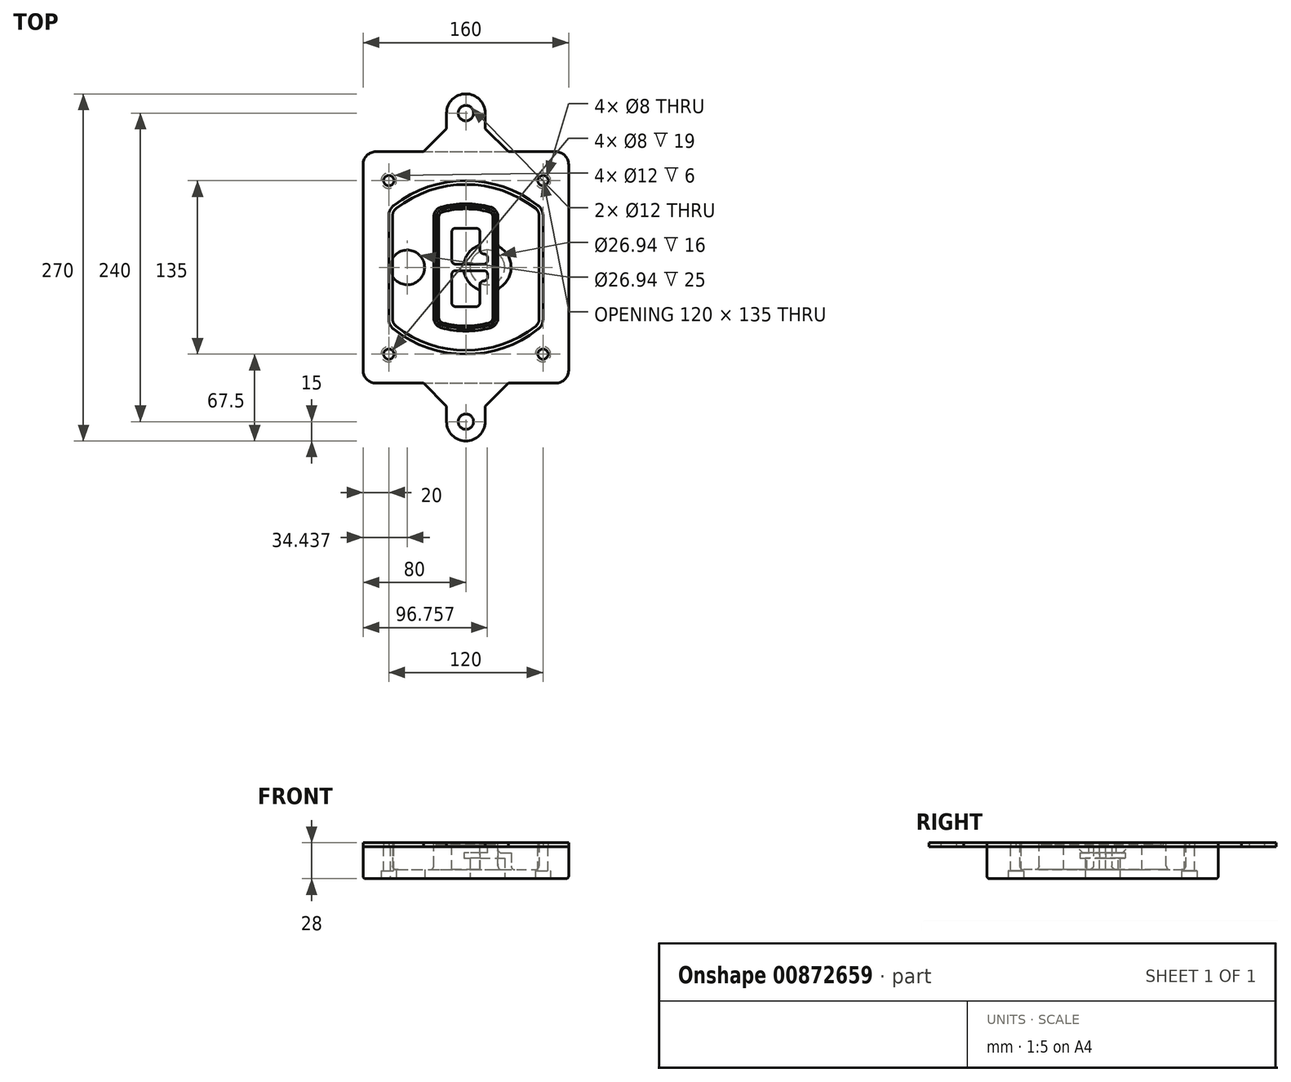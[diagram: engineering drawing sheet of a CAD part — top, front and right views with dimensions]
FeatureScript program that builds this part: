
annotation { "Feature Type Name" : "Feature", "Feature Type Description" : "" }
export const myFeature = defineFeature(function(context is Context, id is Id, definition is map)
    precondition{}
    {
        {
            var Q0;
            Q0=qCreatedBy(makeId("Top.planeOp"),FACE);
            var sketch = newSketch(context, id + "F0", { "sketchPlane" : qUnion([Q0])});
            skPoint(sketch, "E0.rect.middle", {"position": v(0, 0) * mm});
            skLineSegment(sketch, "E1.bottom", {"start": v(-70, -90) * mm, "end": v(70, -90) * mm});
            skLineSegment(sketch, "E1.top", {"start": v(-70, 90) * mm, "end": v(70, 90) * mm});
            skLineSegment(sketch, "E1.left", {"start": v(-80, -80) * mm, "end": v(-80, 80) * mm});
            skLineSegment(sketch, "E1.right", {"start": v(80, -80) * mm, "end": v(80, 80) * mm});
            skLineSegment(sketch, "E2", {"start": v(-80, 90) * mm, "end": v(80, -90) * mm, "construction": true});
            skLineSegment(sketch, "E3", {"start": v(80, 90) * mm, "end": v(-80, -90) * mm, "construction": true});
            skCircle(sketch, "E4", {"center": v(-60, 67.5) * mm, "radius": 4 * mm});
            skCircle(sketch, "E5", {"center": v(60, 67.5) * mm, "radius": 4 * mm});
            skCircle(sketch, "E6", {"center": v(60, -67.5) * mm, "radius": 4 * mm});
            skCircle(sketch, "E7", {"center": v(-60, -67.5) * mm, "radius": 4 * mm});
            skLineSegment(sketch, "E8", {"start": v(-60, 67.5) * mm, "end": v(60, 67.5) * mm, "construction": true});
            skLineSegment(sketch, "E9", {"start": v(60, 67.5) * mm, "end": v(60, -67.5) * mm, "construction": true});
            skLineSegment(sketch, "E10", {"start": v(60, -67.5) * mm, "end": v(-60, -67.5) * mm, "construction": true});
            skLineSegment(sketch, "E11", {"start": v(-60, -67.5) * mm, "end": v(-60, 67.5) * mm, "construction": true});
            skLineSegment(sketch, "E12", {"start": v(-60, 40.3) * mm, "end": v(-60, -40.3) * mm});
            skLineSegment(sketch, "E13", {"start": v(60, 40.3) * mm, "end": v(60, -40.3) * mm});
            skArc(sketch, "E14", {"start": v(56.15, 48.18) * mm, "mid": v(0, 67.5) * mm, "end": v(-56.15, 48.18) * mm});
            skArc(sketch, "E15", {"start": v(-56.15, -48.18) * mm, "mid": v(0, -67.5) * mm, "end": v(56.15, -48.18) * mm});
            skLineSegment(sketch, "E16", {"start": v(-60, 0) * mm, "end": v(60, 0) * mm, "construction": true});
            skPoint(sketch, "E17.visualSharp", {"position": v(-60, -45) * mm});
            skArc(sketch, "E17.filletArc", {"start": v(-60, -40.3) * mm, "mid": v(-58.99, -44.68) * mm, "end": v(-56.15, -48.18) * mm});
            skPoint(sketch, "E18.visualSharp", {"position": v(-60, 45) * mm});
            skArc(sketch, "E18.filletArc", {"start": v(-56.15, 48.18) * mm, "mid": v(-58.99, 44.68) * mm, "end": v(-60, 40.3) * mm});
            skPoint(sketch, "E19.visualSharp", {"position": v(60, 45) * mm});
            skArc(sketch, "E19.filletArc", {"start": v(60, 40.3) * mm, "mid": v(58.99, 44.68) * mm, "end": v(56.15, 48.18) * mm});
            skPoint(sketch, "E20.visualSharp", {"position": v(60, -45) * mm});
            skArc(sketch, "E20.filletArc", {"start": v(56.15, -48.18) * mm, "mid": v(58.99, -44.68) * mm, "end": v(60, -40.3) * mm});
            skPoint(sketch, "E21.visualSharp", {"position": v(-80, 90) * mm});
            skArc(sketch, "E21.filletArc", {"start": v(-70, 90) * mm, "mid": v(-77.07, 87.07) * mm, "end": v(-80, 80) * mm});
            skPoint(sketch, "E22.visualSharp", {"position": v(80, 90) * mm});
            skArc(sketch, "E22.filletArc", {"start": v(80, 80) * mm, "mid": v(77.07, 87.07) * mm, "end": v(70, 90) * mm});
            skPoint(sketch, "E23.visualSharp", {"position": v(80, -90) * mm});
            skArc(sketch, "E23.filletArc", {"start": v(70, -90) * mm, "mid": v(77.07, -87.07) * mm, "end": v(80, -80) * mm});
            skPoint(sketch, "E24.visualSharp", {"position": v(-80, -90) * mm});
            skArc(sketch, "E24.filletArc", {"start": v(-80, -80) * mm, "mid": v(-77.07, -87.07) * mm, "end": v(-70, -90) * mm});
            skArc(sketch, "E25.0", {"start": v(57, 40.3) * mm, "mid": v(56.3, 43.36) * mm, "end": v(54.3, 45.81) * mm});
            skLineSegment(sketch, "E25.1", {"start": v(57, 40.3) * mm, "end": v(57, -40.3) * mm});
            skArc(sketch, "E25.2", {"start": v(54.3, -45.81) * mm, "mid": v(56.3, -43.36) * mm, "end": v(57, -40.3) * mm});
            skArc(sketch, "E25.3", {"start": v(-54.3, -45.81) * mm, "mid": v(0, -64.5) * mm, "end": v(54.3, -45.81) * mm});
            skArc(sketch, "E25.4", {"start": v(-57, -40.3) * mm, "mid": v(-56.3, -43.36) * mm, "end": v(-54.3, -45.81) * mm});
            skArc(sketch, "E25.5", {"start": v(54.3, 45.81) * mm, "mid": v(0, 64.5) * mm, "end": v(-54.3, 45.81) * mm});
            skLineSegment(sketch, "E25.6", {"start": v(-57, 40.3) * mm, "end": v(-57, -40.3) * mm});
            skArc(sketch, "E25.7", {"start": v(-54.3, 45.81) * mm, "mid": v(-56.3, 43.36) * mm, "end": v(-57, 40.3) * mm});
            skArc(sketch, "E26.0", {"start": v(-58.62, 51.33) * mm, "mid": v(-62.58, 46.43) * mm, "end": v(-64, 40.3) * mm});
            skArc(sketch, "E26.1", {"start": v(58.62, 51.33) * mm, "mid": v(0, 71.5) * mm, "end": v(-58.62, 51.33) * mm});
            skArc(sketch, "E26.2", {"start": v(64, 40.3) * mm, "mid": v(62.58, 46.43) * mm, "end": v(58.62, 51.33) * mm});
            skLineSegment(sketch, "E26.3", {"start": v(64, 40.3) * mm, "end": v(64, -40.3) * mm});
            skArc(sketch, "E26.4", {"start": v(58.62, -51.33) * mm, "mid": v(62.58, -46.43) * mm, "end": v(64, -40.3) * mm});
            skLineSegment(sketch, "E26.5", {"start": v(-64, 40.3) * mm, "end": v(-64, -40.3) * mm});
            skArc(sketch, "E26.6", {"start": v(-58.62, -51.33) * mm, "mid": v(0, -71.5) * mm, "end": v(58.62, -51.33) * mm});
            skArc(sketch, "E26.7", {"start": v(-64, -40.3) * mm, "mid": v(-62.58, -46.43) * mm, "end": v(-58.62, -51.33) * mm});
            skSolve(sketch);
        }
        {
            var Q0;
            Q0=makeQuery(id+"F0.imprint","IMPRINT",FACE,{"disambiguationData":[TD([[makeQuery(id+"F0.imprint","IMPRINT",EDGE,{"derivedFrom":sQuery(id+"F0.wireOp",EDGE,"E1.bottom")}),1.0]])]});
            var Q1;
            Q1=makeQuery(id+"F0.imprint","IMPRINT",FACE,{"disambiguationData":[TD([[makeQuery(id+"F0.imprint","IMPRINT",EDGE,{"derivedFrom":sQuery(id+"F0.wireOp",EDGE,"E12")}),1.0]])]});
            var Q2;
            Q2=makeQuery(id+"F0.imprint","IMPRINT",FACE,{"disambiguationData":[TD([[makeQuery(id+"F0.imprint","IMPRINT",EDGE,{"derivedFrom":sQuery(id+"F0.wireOp",EDGE,"E25.0")}),1.0]])]});
            var Q3;
            Q3=makeQuery(id+"F0.imprint","IMPRINT",FACE,{"disambiguationData":[TD([[makeQuery(id+"F0.imprint","IMPRINT",EDGE,{"derivedFrom":sQuery(id+"F0.wireOp",EDGE,"E12")}),-1.0]])]});
            extrude(context, id + "F1", {"entities" : qUnion([Q0, Q1, Q2, Q3]), "oppositeDirection" : true, "depth" : 25 * mm});
        }
        {
            var Q0;
            Q0=makeQuery(id+"F0.imprint","IMPRINT",FACE,{"disambiguationData":[TD([[makeQuery(id+"F0.imprint","IMPRINT",EDGE,{"derivedFrom":sQuery(id+"F0.wireOp",EDGE,"E12")}),1.0]])]});
            extrude(context, id + "F2", {"entities" : qUnion([Q0]), "operationType" : NewBodyOperationType.ADD, "depth" : 3 * mm});
        }
        {
            var Q0;
            Q0=makeQuery(id+"F0.imprint","IMPRINT",FACE,{"disambiguationData":[TD([[makeQuery(id+"F0.imprint","IMPRINT",EDGE,{"derivedFrom":sQuery(id+"F0.wireOp",EDGE,"E25.0")}),1.0]])]});
            extrude(context, id + "F3", {"entities" : qUnion([Q0]), "operationType" : NewBodyOperationType.REMOVE, "oppositeDirection" : true, "depth" : 18 * mm});
        }
        {
            var Q0;
            Q0=makeQuery(id+"F2.opExtrude","CAP_FACE",FACE,{"disambiguationData":[OSD([sQuery(id+"F0.wireOp",EDGE,"E12"),sQuery(id+"F0.wireOp",EDGE,"E13"),sQuery(id+"F0.wireOp",EDGE,"E14"),sQuery(id+"F0.wireOp",EDGE,"E15"),sQuery(id+"F0.wireOp",EDGE,"E17.filletArc"),sQuery(id+"F0.wireOp",EDGE,"E18.filletArc"),sQuery(id+"F0.wireOp",EDGE,"E19.filletArc"),sQuery(id+"F0.wireOp",EDGE,"E20.filletArc"),sQuery(id+"F0.wireOp",EDGE,"E25.0"),sQuery(id+"F0.wireOp",EDGE,"E25.1"),sQuery(id+"F0.wireOp",EDGE,"E25.2"),sQuery(id+"F0.wireOp",EDGE,"E25.3"),sQuery(id+"F0.wireOp",EDGE,"E25.4"),sQuery(id+"F0.wireOp",EDGE,"E25.5"),sQuery(id+"F0.wireOp",EDGE,"E25.6"),sQuery(id+"F0.wireOp",EDGE,"E25.7")])],"isStart":false});
            var sketch = newSketch(context, id + "F4", { "sketchPlane" : qUnion([Q0])});
            skArc(sketch, "E27.0", {"start": v(-19.08, -46.97) * mm, "mid": v(0, -49.5) * mm, "end": v(19.08, -46.97) * mm});
            skArc(sketch, "E28.0", {"start": v(19.08, 46.97) * mm, "mid": v(0, 49.5) * mm, "end": v(-19.08, 46.97) * mm});
            skLineSegment(sketch, "E29", {"start": v(-25, 39.25) * mm, "end": v(-25, -39.25) * mm});
            skLineSegment(sketch, "E30", {"start": v(25, 39.25) * mm, "end": v(25, -39.25) * mm});
            skLineSegment(sketch, "E31", {"start": v(-25, 45.1) * mm, "end": v(25, 45.1) * mm, "construction": true});
            skLineSegment(sketch, "E32", {"start": v(-25, -45.1) * mm, "end": v(25, -45.1) * mm, "construction": true});
            skPoint(sketch, "E33.visualSharp", {"position": v(-25, 45.1) * mm});
            skArc(sketch, "E33.filletArc", {"start": v(-19.08, 46.97) * mm, "mid": v(-23.35, 44.11) * mm, "end": v(-25, 39.25) * mm});
            skPoint(sketch, "E34.visualSharp", {"position": v(25, 45.1) * mm});
            skArc(sketch, "E34.filletArc", {"start": v(25, 39.25) * mm, "mid": v(23.35, 44.11) * mm, "end": v(19.08, 46.97) * mm});
            skPoint(sketch, "E35.visualSharp", {"position": v(25, -45.1) * mm});
            skArc(sketch, "E35.filletArc", {"start": v(19.08, -46.97) * mm, "mid": v(23.35, -44.11) * mm, "end": v(25, -39.25) * mm});
            skPoint(sketch, "E36.visualSharp", {"position": v(-25, -45.1) * mm});
            skArc(sketch, "E36.filletArc", {"start": v(-25, -39.25) * mm, "mid": v(-23.35, -44.11) * mm, "end": v(-19.08, -46.97) * mm});
            skArc(sketch, "E37.0", {"start": v(54.3, 45.81) * mm, "mid": v(0, 64.5) * mm, "end": v(-54.3, 45.81) * mm});
            skArc(sketch, "E37.1", {"start": v(-54.3, 45.81) * mm, "mid": v(-56.3, 43.36) * mm, "end": v(-57, 40.3) * mm});
            skLineSegment(sketch, "E37.2", {"start": v(-57, 40.3) * mm, "end": v(-57, -40.3) * mm});
            skArc(sketch, "E37.3", {"start": v(-57, -40.3) * mm, "mid": v(-56.3, -43.36) * mm, "end": v(-54.3, -45.81) * mm});
            skArc(sketch, "E37.4", {"start": v(-54.3, -45.81) * mm, "mid": v(0, -64.5) * mm, "end": v(54.3, -45.81) * mm});
            skArc(sketch, "E37.5", {"start": v(54.3, -45.81) * mm, "mid": v(56.3, -43.36) * mm, "end": v(57, -40.3) * mm});
            skLineSegment(sketch, "E37.6", {"start": v(57, 40.3) * mm, "end": v(57, -40.3) * mm});
            skArc(sketch, "E37.7", {"start": v(57, 40.3) * mm, "mid": v(56.3, 43.36) * mm, "end": v(54.3, 45.81) * mm});
            skLineSegment(sketch, "E38.0", {"start": v(23, 39.25) * mm, "end": v(23, -39.25) * mm});
            skArc(sketch, "E38.1", {"start": v(18.56, -45.04) * mm, "mid": v(21.76, -42.9) * mm, "end": v(23, -39.25) * mm});
            skArc(sketch, "E38.2", {"start": v(-18.56, -45.04) * mm, "mid": v(0, -47.5) * mm, "end": v(18.56, -45.04) * mm});
            skArc(sketch, "E38.3", {"start": v(-23, -39.25) * mm, "mid": v(-21.76, -42.9) * mm, "end": v(-18.56, -45.04) * mm});
            skLineSegment(sketch, "E38.4", {"start": v(-23, 39.25) * mm, "end": v(-23, -39.25) * mm});
            skArc(sketch, "E38.5", {"start": v(23, 39.25) * mm, "mid": v(21.76, 42.9) * mm, "end": v(18.56, 45.04) * mm});
            skArc(sketch, "E38.6", {"start": v(-18.56, 45.04) * mm, "mid": v(-21.76, 42.9) * mm, "end": v(-23, 39.25) * mm});
            skArc(sketch, "E38.7", {"start": v(18.56, 45.04) * mm, "mid": v(0, 47.5) * mm, "end": v(-18.56, 45.04) * mm});
            skArc(sketch, "E39.0", {"start": v(21, 39.25) * mm, "mid": v(20.18, 41.68) * mm, "end": v(18.04, 43.1) * mm});
            skLineSegment(sketch, "E39.1", {"start": v(21, 39.25) * mm, "end": v(21, -39.25) * mm});
            skArc(sketch, "E39.2", {"start": v(18.04, -43.1) * mm, "mid": v(20.18, -41.68) * mm, "end": v(21, -39.25) * mm});
            skArc(sketch, "E39.3", {"start": v(-18.04, -43.1) * mm, "mid": v(0, -45.5) * mm, "end": v(18.04, -43.1) * mm});
            skArc(sketch, "E39.4", {"start": v(-21, -39.25) * mm, "mid": v(-20.18, -41.68) * mm, "end": v(-18.04, -43.1) * mm});
            skArc(sketch, "E39.5", {"start": v(18.04, 43.1) * mm, "mid": v(0, 45.5) * mm, "end": v(-18.04, 43.1) * mm});
            skLineSegment(sketch, "E39.6", {"start": v(-21, 39.25) * mm, "end": v(-21, -39.25) * mm});
            skArc(sketch, "E39.7", {"start": v(-18.04, 43.1) * mm, "mid": v(-20.18, 41.68) * mm, "end": v(-21, 39.25) * mm});
            skLineSegment(sketch, "E40", {"start": v(-25, 0) * mm, "end": v(25, 0) * mm, "construction": true});
            skLineSegment(sketch, "E41", {"start": v(-11, 5.5) * mm, "end": v(-11, 27.5) * mm});
            skLineSegment(sketch, "E42", {"start": v(-8, 30.5) * mm, "end": v(8, 30.5) * mm});
            skLineSegment(sketch, "E43", {"start": v(11, 27.5) * mm, "end": v(11, 13.5) * mm});
            skLineSegment(sketch, "E44", {"start": v(14, 10.5) * mm, "end": v(14, 10.5) * mm});
            skLineSegment(sketch, "E45", {"start": v(17, 7.5) * mm, "end": v(17, 5.5) * mm});
            skLineSegment(sketch, "E46", {"start": v(14, 2.5) * mm, "end": v(-8, 2.5) * mm});
            skPoint(sketch, "E47.visualSharp", {"position": v(-11, 30.5) * mm});
            skArc(sketch, "E47.filletArc", {"start": v(-8, 30.5) * mm, "mid": v(-10.12, 29.62) * mm, "end": v(-11, 27.5) * mm});
            skPoint(sketch, "E48.visualSharp", {"position": v(11, 30.5) * mm});
            skArc(sketch, "E48.filletArc", {"start": v(11, 27.5) * mm, "mid": v(10.12, 29.62) * mm, "end": v(8, 30.5) * mm});
            skPoint(sketch, "E49.visualSharp", {"position": v(11, 10.5) * mm});
            skArc(sketch, "E49.filletArc", {"start": v(11, 13.5) * mm, "mid": v(11.88, 11.38) * mm, "end": v(14, 10.5) * mm});
            skPoint(sketch, "E50.visualSharp", {"position": v(17, 10.5) * mm});
            skArc(sketch, "E50.filletArc", {"start": v(17, 7.5) * mm, "mid": v(16.12, 9.62) * mm, "end": v(14, 10.5) * mm});
            skPoint(sketch, "E51.visualSharp", {"position": v(17, 2.5) * mm});
            skArc(sketch, "E51.filletArc", {"start": v(14, 2.5) * mm, "mid": v(16.12, 3.38) * mm, "end": v(17, 5.5) * mm});
            skPoint(sketch, "E52.visualSharp", {"position": v(-11, 2.5) * mm});
            skArc(sketch, "E52.filletArc", {"start": v(-11, 5.5) * mm, "mid": v(-10.12, 3.38) * mm, "end": v(-8, 2.5) * mm});
            skLineSegment(sketch, "E53.0.MirrorCS", {"start": v(14, -2.5) * mm, "end": v(-8, -2.5) * mm});
            skArc(sketch, "E54.0.MirrorCS", {"start": v(-11, -5.5) * mm, "mid": v(-10.12, -3.38) * mm, "end": v(-8, -2.5) * mm});
            skLineSegment(sketch, "E55.0.MirrorCS", {"start": v(-11, -5.5) * mm, "end": v(-11, -27.5) * mm});
            skArc(sketch, "E56.0.MirrorCS", {"start": v(-8, -30.5) * mm, "mid": v(-10.12, -29.62) * mm, "end": v(-11, -27.5) * mm});
            skLineSegment(sketch, "E57.0.MirrorCS", {"start": v(-8, -30.5) * mm, "end": v(8, -30.5) * mm});
            skArc(sketch, "E58.0.MirrorCS", {"start": v(11, -27.5) * mm, "mid": v(10.12, -29.62) * mm, "end": v(8, -30.5) * mm});
            skLineSegment(sketch, "E59.0.MirrorCS", {"start": v(11, -27.5) * mm, "end": v(11, -13.5) * mm});
            skArc(sketch, "E60.0.MirrorCS", {"start": v(11, -13.5) * mm, "mid": v(11.88, -11.38) * mm, "end": v(14, -10.5) * mm});
            skArc(sketch, "E61.0.MirrorCS", {"start": v(17, -7.5) * mm, "mid": v(16.12, -9.62) * mm, "end": v(14, -10.5) * mm});
            skLineSegment(sketch, "E62.0.MirrorCS", {"start": v(17, -7.5) * mm, "end": v(17, -5.5) * mm});
            skArc(sketch, "E63.0.MirrorCS", {"start": v(14, -2.5) * mm, "mid": v(16.12, -3.38) * mm, "end": v(17, -5.5) * mm});
            skSolve(sketch);
        }
        {
            var Q0;
            Q0=makeQuery(id+"F4.imprint","IMPRINT",FACE,{"disambiguationData":[TD([[makeQuery(id+"F4.imprint","IMPRINT",EDGE,{"derivedFrom":sQuery(id+"F4.wireOp",EDGE,"E27.0")}),1.0]])]});
            var Q1;
            Q1=makeQuery(id+"F4.imprint","IMPRINT",FACE,{"disambiguationData":[TD([[makeQuery(id+"F4.imprint","IMPRINT",EDGE,{"derivedFrom":sQuery(id+"F4.wireOp",EDGE,"E38.0")}),-1.0]])]});
            var Q2;
            Q2=makeQuery(id+"F4.imprint","IMPRINT",FACE,{"disambiguationData":[TD([[makeQuery(id+"F4.imprint","IMPRINT",EDGE,{"derivedFrom":sQuery(id+"F4.wireOp",EDGE,"E39.0")}),1.0]])]});
            extrude(context, id + "F5", {"entities" : qUnion([Q0, Q1, Q2]), "operationType" : NewBodyOperationType.ADD, "endBound" : BoundingType.UP_TO_NEXT, "oppositeDirection" : true, "depth" : 25 * mm});
        }
        {
            var Q0;
            Q0=makeQuery(id+"F4.imprint","IMPRINT",FACE,{"disambiguationData":[TD([[makeQuery(id+"F4.imprint","IMPRINT",EDGE,{"derivedFrom":sQuery(id+"F4.wireOp",EDGE,"E38.0")}),-1.0]])]});
            extrude(context, id + "F6", {"entities" : qUnion([Q0]), "operationType" : NewBodyOperationType.REMOVE, "oppositeDirection" : true, "depth" : 2 * mm});
        }
        {
            var Q0;
            Q0=makeQuery(id+"F1.opExtrude","CAP_FACE",FACE,{"disambiguationData":[OSD([sQuery(id+"F0.wireOp",EDGE,"E1.bottom"),sQuery(id+"F0.wireOp",EDGE,"E1.top"),sQuery(id+"F0.wireOp",EDGE,"E1.left"),sQuery(id+"F0.wireOp",EDGE,"E1.right"),sQuery(id+"F0.wireOp",EDGE,"E4"),sQuery(id+"F0.wireOp",EDGE,"E5"),sQuery(id+"F0.wireOp",EDGE,"E6"),sQuery(id+"F0.wireOp",EDGE,"E7"),sQuery(id+"F0.wireOp",EDGE,"E21.filletArc"),sQuery(id+"F0.wireOp",EDGE,"E22.filletArc"),sQuery(id+"F0.wireOp",EDGE,"E23.filletArc"),sQuery(id+"F0.wireOp",EDGE,"E24.filletArc")])],"isStart":false});
            var sketch = newSketch(context, id + "F7", { "sketchPlane" : qUnion([Q0])});
            skCircle(sketch, "E64", {"center": v(16.76, 0) * mm, "radius": 13.47 * mm});
            skCircle(sketch, "E65", {"center": v(-45.56, 0) * mm, "radius": 13.47 * mm});
            skLineSegment(sketch, "E66", {"start": v(80, 0) * mm, "end": v(-80, 0) * mm});
            skCircle(sketch, "E67", {"center": v(16.76, 0) * mm, "radius": 18.47 * mm});
            skCircle(sketch, "E68", {"center": v(60, -67.5) * mm, "radius": 6 * mm});
            skCircle(sketch, "E69", {"center": v(-60, -67.5) * mm, "radius": 6 * mm});
            skCircle(sketch, "E70", {"center": v(-60, 67.5) * mm, "radius": 6 * mm});
            skCircle(sketch, "E71", {"center": v(60, 67.5) * mm, "radius": 6 * mm});
            skSolve(sketch);
        }
        {
            var Q0;
            {var subQ1=sQuery(id+"F7.wireOp",EDGE,"E66");var subQ4=sQuery(id+"F7.wireOp",EDGE,"E64");var subQ6=makeQuery(id+"F7.imprint","INTERSECT",VERTEX,{"disambiguationData":[OD(0.0)],"derivedFrom":[subQ4,subQ1]});Q0=makeQuery(id+"F7.imprint","IMPRINT",FACE,{"disambiguationData":[TD([[makeQuery(id+"F7.imprint","IMPRINT",EDGE,{"disambiguationData":[TD([[subQ6,-1.0]])],"derivedFrom":subQ4}),-1.0]])]});}
            var Q1;
            {var subQ0=sQuery(id+"F7.wireOp",EDGE,"E66");var subQ1=sQuery(id+"F7.wireOp",EDGE,"E64");var subQ3=makeQuery(id+"F7.imprint","INTERSECT",VERTEX,{"disambiguationData":[OD(0.0)],"derivedFrom":[subQ1,subQ0]});Q1=makeQuery(id+"F7.imprint","IMPRINT",FACE,{"disambiguationData":[TD([[makeQuery(id+"F7.imprint","IMPRINT",EDGE,{"disambiguationData":[TD([[subQ3,-1.0]])],"derivedFrom":subQ1}),1.0]])]});}
            var Q2;
            {var subQ0=sQuery(id+"F7.wireOp",EDGE,"E66");var subQ1=sQuery(id+"F7.wireOp",EDGE,"E64");var subQ3=makeQuery(id+"F7.imprint","INTERSECT",VERTEX,{"disambiguationData":[OD(0.0)],"derivedFrom":[subQ1,subQ0]});Q2=makeQuery(id+"F7.imprint","IMPRINT",FACE,{"disambiguationData":[TD([[makeQuery(id+"F7.imprint","IMPRINT",EDGE,{"disambiguationData":[TD([[subQ3,1.0]])],"derivedFrom":subQ1}),1.0]])]});}
            var Q3;
            {var subQ1=sQuery(id+"F7.wireOp",EDGE,"E66");var subQ4=sQuery(id+"F7.wireOp",EDGE,"E64");var subQ6=makeQuery(id+"F7.imprint","INTERSECT",VERTEX,{"disambiguationData":[OD(0.0)],"derivedFrom":[subQ4,subQ1]});Q3=makeQuery(id+"F7.imprint","IMPRINT",FACE,{"disambiguationData":[TD([[makeQuery(id+"F7.imprint","IMPRINT",EDGE,{"disambiguationData":[TD([[subQ6,1.0]])],"derivedFrom":subQ4}),-1.0]])]});}
            extrude(context, id + "F8", {"entities" : qUnion([Q0, Q1, Q2, Q3]), "operationType" : NewBodyOperationType.ADD, "oppositeDirection" : true, "depth" : 20 * mm});
        }
        {
            var Q0;
            {var subQ0=sQuery(id+"F7.wireOp",EDGE,"E66");var subQ1=sQuery(id+"F7.wireOp",EDGE,"E64");var subQ3=makeQuery(id+"F7.imprint","INTERSECT",VERTEX,{"disambiguationData":[OD(0.0)],"derivedFrom":[subQ1,subQ0]});Q0=makeQuery(id+"F7.imprint","IMPRINT",FACE,{"disambiguationData":[TD([[makeQuery(id+"F7.imprint","IMPRINT",EDGE,{"disambiguationData":[TD([[subQ3,-1.0]])],"derivedFrom":subQ1}),1.0]])]});}
            var Q1;
            {var subQ0=sQuery(id+"F7.wireOp",EDGE,"E66");var subQ1=sQuery(id+"F7.wireOp",EDGE,"E64");var subQ3=makeQuery(id+"F7.imprint","INTERSECT",VERTEX,{"disambiguationData":[OD(0.0)],"derivedFrom":[subQ1,subQ0]});Q1=makeQuery(id+"F7.imprint","IMPRINT",FACE,{"disambiguationData":[TD([[makeQuery(id+"F7.imprint","IMPRINT",EDGE,{"disambiguationData":[TD([[subQ3,1.0]])],"derivedFrom":subQ1}),1.0]])]});}
            extrude(context, id + "F9", {"entities" : qUnion([Q0, Q1]), "operationType" : NewBodyOperationType.REMOVE, "oppositeDirection" : true, "depth" : 16 * mm});
        }
        {
            var Q0;
            {var subQ0=sQuery(id+"F7.wireOp",EDGE,"E66");var subQ1=sQuery(id+"F7.wireOp",EDGE,"E65");var subQ3=makeQuery(id+"F7.imprint","INTERSECT",VERTEX,{"disambiguationData":[OD(0.0)],"derivedFrom":[subQ1,subQ0]});Q0=makeQuery(id+"F7.imprint","IMPRINT",FACE,{"disambiguationData":[TD([[makeQuery(id+"F7.imprint","IMPRINT",EDGE,{"disambiguationData":[TD([[subQ3,-1.0]])],"derivedFrom":subQ1}),1.0]])]});}
            var Q1;
            {var subQ0=sQuery(id+"F7.wireOp",EDGE,"E66");var subQ1=sQuery(id+"F7.wireOp",EDGE,"E65");var subQ3=makeQuery(id+"F7.imprint","INTERSECT",VERTEX,{"disambiguationData":[OD(0.0)],"derivedFrom":[subQ1,subQ0]});Q1=makeQuery(id+"F7.imprint","IMPRINT",FACE,{"disambiguationData":[TD([[makeQuery(id+"F7.imprint","IMPRINT",EDGE,{"disambiguationData":[TD([[subQ3,1.0]])],"derivedFrom":subQ1}),1.0]])]});}
            extrude(context, id + "F10", {"entities" : qUnion([Q0, Q1]), "operationType" : NewBodyOperationType.REMOVE, "oppositeDirection" : true, "depth" : 25 * mm});
        }
        {
            var Q0;
            Q0=makeQuery(id+"F7.imprint","IMPRINT",FACE,{"disambiguationData":[TD([[makeQuery(id+"F7.imprint","IMPRINT",EDGE,{"derivedFrom":sQuery(id+"F7.wireOp",EDGE,"E68")}),1.0]])]});
            var Q1;
            Q1=makeQuery(id+"F7.imprint","IMPRINT",FACE,{"disambiguationData":[TD([[makeQuery(id+"F7.imprint","IMPRINT",EDGE,{"derivedFrom":makeQuery(id+"F1.opExtrude","CAP_EDGE",EDGE,{"disambiguationData":[OSD([sQuery(id+"F0.wireOp",EDGE,"E5")])],"isStart":false})}),-1.0]])]});
            var Q2;
            Q2=makeQuery(id+"F7.imprint","IMPRINT",FACE,{"disambiguationData":[TD([[makeQuery(id+"F7.imprint","IMPRINT",EDGE,{"derivedFrom":sQuery(id+"F7.wireOp",EDGE,"E69")}),1.0]])]});
            var Q3;
            Q3=makeQuery(id+"F7.imprint","IMPRINT",FACE,{"disambiguationData":[TD([[makeQuery(id+"F7.imprint","IMPRINT",EDGE,{"derivedFrom":makeQuery(id+"F1.opExtrude","CAP_EDGE",EDGE,{"disambiguationData":[OSD([sQuery(id+"F0.wireOp",EDGE,"E4")])],"isStart":false})}),-1.0]])]});
            var Q4;
            Q4=makeQuery(id+"F7.imprint","IMPRINT",FACE,{"disambiguationData":[TD([[makeQuery(id+"F7.imprint","IMPRINT",EDGE,{"derivedFrom":sQuery(id+"F7.wireOp",EDGE,"E70")}),1.0]])]});
            var Q5;
            Q5=makeQuery(id+"F7.imprint","IMPRINT",FACE,{"disambiguationData":[TD([[makeQuery(id+"F7.imprint","IMPRINT",EDGE,{"derivedFrom":makeQuery(id+"F1.opExtrude","CAP_EDGE",EDGE,{"disambiguationData":[OSD([sQuery(id+"F0.wireOp",EDGE,"E7")])],"isStart":false})}),-1.0]])]});
            var Q6;
            Q6=makeQuery(id+"F7.imprint","IMPRINT",FACE,{"disambiguationData":[TD([[makeQuery(id+"F7.imprint","IMPRINT",EDGE,{"derivedFrom":sQuery(id+"F7.wireOp",EDGE,"E71")}),1.0]])]});
            var Q7;
            Q7=makeQuery(id+"F7.imprint","IMPRINT",FACE,{"disambiguationData":[TD([[makeQuery(id+"F7.imprint","IMPRINT",EDGE,{"derivedFrom":makeQuery(id+"F1.opExtrude","CAP_EDGE",EDGE,{"disambiguationData":[OSD([sQuery(id+"F0.wireOp",EDGE,"E6")])],"isStart":false})}),-1.0]])]});
            extrude(context, id + "F11", {"entities" : qUnion([Q0, Q1, Q2, Q3, Q4, Q5, Q6, Q7]), "operationType" : NewBodyOperationType.REMOVE, "oppositeDirection" : true, "depth" : 6 * mm});
        }
        {
            var Q0;
            Q0=makeQuery(id+"F9.boolean.opBoolean","COPY",FACE,{"derivedFrom":makeQuery(id+"F9.opExtrude","CAP_FACE",FACE,{"disambiguationData":[OSD([sQuery(id+"F7.wireOp",EDGE,"E64")])],"isStart":false})});
            var sketch = newSketch(context, id + "F12", { "sketchPlane" : qUnion([Q0])});
            skArc(sketch, "E72.0", {"start": v(11, 17.55) * mm, "mid": v(2.57, 11.82) * mm, "end": v(-1.54, 2.5) * mm});
            skArc(sketch, "E72.1", {"start": v(-1.54, -2.5) * mm, "mid": v(2.57, -11.82) * mm, "end": v(11, -17.55) * mm});
            skLineSegment(sketch, "E73", {"start": v(-1.54, -2.5) * mm, "end": v(14, -2.5) * mm});
            skLineSegment(sketch, "E74.0", {"start": v(14, 2.5) * mm, "end": v(-1.54, 2.5) * mm});
            skArc(sketch, "E74.1", {"start": v(14, 2.5) * mm, "mid": v(16.12, 3.38) * mm, "end": v(17, 5.5) * mm});
            skLineSegment(sketch, "E74.2", {"start": v(17, 7.5) * mm, "end": v(17, 5.5) * mm});
            skArc(sketch, "E74.3", {"start": v(17, 7.5) * mm, "mid": v(16.12, 9.62) * mm, "end": v(14, 10.5) * mm});
            skArc(sketch, "E74.4", {"start": v(11, 13.5) * mm, "mid": v(11.88, 11.38) * mm, "end": v(14, 10.5) * mm});
            skLineSegment(sketch, "E74.5", {"start": v(11, 17.55) * mm, "end": v(11, 13.5) * mm});
            skLineSegment(sketch, "E74.7", {"start": v(14, -2.5) * mm, "end": v(-1.54, -2.5) * mm});
            skArc(sketch, "E74.8", {"start": v(14, -2.5) * mm, "mid": v(16.12, -3.38) * mm, "end": v(17, -5.5) * mm});
            skLineSegment(sketch, "E74.9", {"start": v(17, -7.5) * mm, "end": v(17, -5.5) * mm});
            skArc(sketch, "E74.10", {"start": v(17, -7.5) * mm, "mid": v(16.12, -9.62) * mm, "end": v(14, -10.5) * mm});
            skArc(sketch, "E74.11", {"start": v(11, -13.5) * mm, "mid": v(11.88, -11.38) * mm, "end": v(14, -10.5) * mm});
            skLineSegment(sketch, "E74.12", {"start": v(11, -17.55) * mm, "end": v(11, -13.5) * mm});
            skPoint(sketch, "E75.orphan", {"position": v(11, -27.5) * mm});
            skPoint(sketch, "E76.orphan", {"position": v(-8, -2.5) * mm});
            skPoint(sketch, "E77.orphan", {"position": v(-8, 2.5) * mm});
            skPoint(sketch, "E78.orphan", {"position": v(11, 27.5) * mm});
            skSolve(sketch);
        }
        {
            var Q0;
            {var subQ7=sQuery(id+"F12.wireOp",EDGE,"E72.0");var subQ14=sQuery(id+"F12.wireOp",EDGE,"E72.1");var subQ16=sQuery(id+"F12.wireOp",EDGE,"E74.1");var subQ18=sQuery(id+"F12.wireOp",EDGE,"E74.8");Q0=qUnion([makeQuery(id+"F12.imprint","IMPRINT",FACE,{"disambiguationData":[TD([[makeQuery(id+"F12.imprint","IMPRINT",EDGE,{"derivedFrom":subQ7}),1.0]])]}),makeQuery(id+"F12.imprint","IMPRINT",FACE,{"disambiguationData":[TD([[makeQuery(id+"F12.imprint","IMPRINT",EDGE,{"derivedFrom":subQ14}),1.0]])]}),makeQuery(id+"F12.imprint","IMPRINT",FACE,{"disambiguationData":[TD([[makeQuery(id+"F12.imprint","IMPRINT",EDGE,{"derivedFrom":subQ16}),1.0]])]}),makeQuery(id+"F12.imprint","IMPRINT",FACE,{"disambiguationData":[TD([[makeQuery(id+"F12.imprint","IMPRINT",EDGE,{"derivedFrom":subQ18}),-1.0]])]})]);}
            var Q1;
            Q1=makeQuery(id+"F5.boolean.opBoolean","SPLIT",FACE,{"disambiguationData":[TD([makeQuery(id+"F5.opExtrude","SWEPT_FACE",FACE,{"disambiguationData":[OSD([sQuery(id+"F4.wireOp",EDGE,"E41")])]})])],"derivedFrom":makeQuery(id+"F3.boolean.opBoolean","COPY",FACE,{"derivedFrom":makeQuery(id+"F3.opExtrude","CAP_FACE",FACE,{"disambiguationData":[OSD([sQuery(id+"F0.wireOp",EDGE,"E25.0"),sQuery(id+"F0.wireOp",EDGE,"E25.1"),sQuery(id+"F0.wireOp",EDGE,"E25.2"),sQuery(id+"F0.wireOp",EDGE,"E25.3"),sQuery(id+"F0.wireOp",EDGE,"E25.4"),sQuery(id+"F0.wireOp",EDGE,"E25.5"),sQuery(id+"F0.wireOp",EDGE,"E25.6"),sQuery(id+"F0.wireOp",EDGE,"E25.7")])],"isStart":false})})});
            extrude(context, id + "F13", {"entities" : qUnion([Q0]), "operationType" : NewBodyOperationType.REMOVE, "endBound" : BoundingType.UP_TO_SURFACE, "endBoundEntityFace" : qUnion([Q1]), "depth" : 25 * mm});
        }
        {
            var Q0;
            Q0=makeQuery(id+"F3.boolean.opBoolean","COPY",EDGE,{"derivedFrom":makeQuery(id+"F3.opExtrude","CAP_EDGE",EDGE,{"disambiguationData":[OSD([sQuery(id+"F0.wireOp",EDGE,"E25.6")])],"isStart":false})});
            var Q1;
            Q1=makeQuery(id+"F8.boolean.opBoolean","INTERSECT",EDGE,{"derivedFrom":[makeQuery(id+"F5.opExtrude","SWEPT_FACE",FACE,{"disambiguationData":[OSD([sQuery(id+"F4.wireOp",EDGE,"E30")])]}),makeQuery(id+"F8.opExtrude","CAP_FACE",FACE,{"disambiguationData":[OSD([sQuery(id+"F7.wireOp",EDGE,"E67")])],"isStart":false})]});
            var Q2;
            Q2=makeQuery(id+"F8.boolean.opBoolean","INTERSECT",EDGE,{"disambiguationData":[OD(1.0)],"derivedFrom":[makeQuery(id+"F5.opExtrude","SWEPT_FACE",FACE,{"disambiguationData":[OSD([sQuery(id+"F4.wireOp",EDGE,"E30")])]}),makeQuery(id+"F8.opExtrude","SWEPT_FACE",FACE,{"disambiguationData":[OSD([sQuery(id+"F7.wireOp",EDGE,"E67")])]})]});
            var Q3;
            {var subQ0=sQuery(id+"F4.wireOp",EDGE,"E30");Q3=makeQuery(id+"F8.boolean.opBoolean","SPLIT",EDGE,{"disambiguationData":[TD([makeQuery(id+"F5.opExtrude","SWEPT_FACE",FACE,{"disambiguationData":[OSD([sQuery(id+"F4.wireOp",EDGE,"E35.filletArc")])]})])],"derivedFrom":makeQuery(id+"F5.opExtrude","CAP_EDGE",EDGE,{"disambiguationData":[OSD([subQ0])],"isStart":false})});}
            var Q4;
            {var subQ0=sQuery(id+"F0.wireOp",EDGE,"E25.7");var subQ1=sQuery(id+"F0.wireOp",EDGE,"E25.1");var subQ2=sQuery(id+"F0.wireOp",EDGE,"E25.6");var subQ3=sQuery(id+"F0.wireOp",EDGE,"E25.5");var subQ4=sQuery(id+"F0.wireOp",EDGE,"E25.4");var subQ5=sQuery(id+"F0.wireOp",EDGE,"E25.0");var subQ6=sQuery(id+"F0.wireOp",EDGE,"E25.2");var subQ7=sQuery(id+"F0.wireOp",EDGE,"E25.3");Q4=makeQuery(id+"F8.boolean.opBoolean","INTERSECT",EDGE,{"derivedFrom":[makeQuery(id+"F5.boolean.opBoolean","SPLIT",FACE,{"disambiguationData":[TD([makeQuery(id+"F2.opExtrude","SWEPT_FACE",FACE,{"disambiguationData":[OSD([subQ5])]})])],"derivedFrom":makeQuery(id+"F3.boolean.opBoolean","COPY",FACE,{"derivedFrom":makeQuery(id+"F3.opExtrude","CAP_FACE",FACE,{"disambiguationData":[OSD([subQ5,subQ1,subQ6,subQ7,subQ4,subQ3,subQ2,subQ0])],"isStart":false})})}),makeQuery(id+"F8.opExtrude","SWEPT_FACE",FACE,{"disambiguationData":[OSD([sQuery(id+"F7.wireOp",EDGE,"E67")])]})]});}
            var Q5;
            Q5=makeQuery(id+"F8.boolean.opBoolean","INTERSECT",EDGE,{"disambiguationData":[OD(0.0)],"derivedFrom":[makeQuery(id+"F5.opExtrude","SWEPT_FACE",FACE,{"disambiguationData":[OSD([sQuery(id+"F4.wireOp",EDGE,"E30")])]}),makeQuery(id+"F8.opExtrude","SWEPT_FACE",FACE,{"disambiguationData":[OSD([sQuery(id+"F7.wireOp",EDGE,"E67")])]})]});
            fillet(context, id + "F14", {"entities" : qUnion([Q0, Q1, Q2, Q3, Q4, Q5]), "radius" : 3 * mm, "tangentPropagation" : true, "allowEdgeOverflow" : false});
        }
        {
            var Q0;
            Q0=makeQuery(id+"F1.opExtrude","CAP_EDGE",EDGE,{"disambiguationData":[OSD([sQuery(id+"F0.wireOp",EDGE,"E1.bottom")])],"isStart":false});
            fillet(context, id + "F15", {"entities" : qUnion([Q0]), "radius" : 2 * mm, "tangentPropagation" : true, "allowEdgeOverflow" : false});
        }
        {
            var Q0;
            {var subQ0=sQuery(id+"F0.wireOp",EDGE,"E21.filletArc");var subQ1=sQuery(id+"F0.wireOp",EDGE,"E7");var subQ2=sQuery(id+"F0.wireOp",EDGE,"E6");var subQ3=sQuery(id+"F0.wireOp",EDGE,"E5");var subQ4=sQuery(id+"F0.wireOp",EDGE,"E4");var subQ5=sQuery(id+"F0.wireOp",EDGE,"E22.filletArc");var subQ6=sQuery(id+"F0.wireOp",EDGE,"E1.bottom");var subQ7=sQuery(id+"F0.wireOp",EDGE,"E1.right");var subQ8=sQuery(id+"F0.wireOp",EDGE,"E1.top");var subQ9=sQuery(id+"F0.wireOp",EDGE,"E1.left");var subQ10=sQuery(id+"F0.wireOp",EDGE,"E23.filletArc");var subQ11=sQuery(id+"F0.wireOp",EDGE,"E24.filletArc");Q0=makeQuery(id+"F2.boolean.opBoolean","SPLIT",FACE,{"disambiguationData":[TD([makeQuery(id+"F1.opExtrude","SWEPT_FACE",FACE,{"disambiguationData":[OSD([subQ6])]})])],"derivedFrom":makeQuery(id+"F1.opExtrude","CAP_FACE",FACE,{"disambiguationData":[OSD([subQ6,subQ8,subQ9,subQ7,subQ4,subQ3,subQ2,subQ1,subQ0,subQ5,subQ10,subQ11])],"isStart":true})});}
            var sketch = newSketch(context, id + "F16", { "sketchPlane" : qUnion([Q0])});
            skArc(sketch, "E79.0", {"start": v(80, 80) * mm, "mid": v(77.07, 87.07) * mm, "end": v(70, 90) * mm});
            skLineSegment(sketch, "E79.1", {"start": v(-70, 90) * mm, "end": v(70, 90) * mm});
            skLineSegment(sketch, "E79.2", {"start": v(80, -80) * mm, "end": v(80, 80) * mm});
            skArc(sketch, "E79.3", {"start": v(70, -90) * mm, "mid": v(77.07, -87.07) * mm, "end": v(80, -80) * mm});
            skLineSegment(sketch, "E79.4", {"start": v(-70, -90) * mm, "end": v(70, -90) * mm});
            skArc(sketch, "E79.5", {"start": v(-80, -80) * mm, "mid": v(-77.07, -87.07) * mm, "end": v(-70, -90) * mm});
            skLineSegment(sketch, "E79.6", {"start": v(-80, -80) * mm, "end": v(-80, 80) * mm});
            skArc(sketch, "E79.7", {"start": v(-70, 90) * mm, "mid": v(-77.07, 87.07) * mm, "end": v(-80, 80) * mm});
            skCircle(sketch, "E79.8", {"center": v(60, 67.5) * mm, "radius": 4 * mm});
            skCircle(sketch, "E79.9", {"center": v(60, -67.5) * mm, "radius": 4 * mm});
            skCircle(sketch, "E79.10", {"center": v(-60, -67.5) * mm, "radius": 4 * mm});
            skCircle(sketch, "E79.11", {"center": v(-60, 67.5) * mm, "radius": 4 * mm});
            skArc(sketch, "E79.12", {"start": v(56.15, 48.18) * mm, "mid": v(0, 67.5) * mm, "end": v(-56.15, 48.18) * mm});
            skArc(sketch, "E79.13", {"start": v(60, 40.3) * mm, "mid": v(58.99, 44.68) * mm, "end": v(56.15, 48.18) * mm});
            skLineSegment(sketch, "E79.14", {"start": v(60, 40.3) * mm, "end": v(60, -40.3) * mm});
            skArc(sketch, "E79.15", {"start": v(56.15, -48.18) * mm, "mid": v(58.99, -44.68) * mm, "end": v(60, -40.3) * mm});
            skArc(sketch, "E79.16", {"start": v(-56.15, -48.18) * mm, "mid": v(0, -67.5) * mm, "end": v(56.15, -48.18) * mm});
            skArc(sketch, "E79.17", {"start": v(-60, -40.3) * mm, "mid": v(-58.99, -44.68) * mm, "end": v(-56.15, -48.18) * mm});
            skLineSegment(sketch, "E79.18", {"start": v(-60, 40.3) * mm, "end": v(-60, -40.3) * mm});
            skArc(sketch, "E79.19", {"start": v(-56.15, 48.18) * mm, "mid": v(-58.99, 44.68) * mm, "end": v(-60, 40.3) * mm});
            skPoint(sketch, "E79.20", {"position": v(77.07, -87.07) * mm});
            skPoint(sketch, "E79.21", {"position": v(-77.07, 87.07) * mm});
            skPoint(sketch, "E79.22", {"position": v(58.99, -44.68) * mm});
            skPoint(sketch, "E79.23", {"position": v(-58.99, 44.68) * mm});
            skCircle(sketch, "E80", {"center": v(0, 120) * mm, "radius": 6 * mm});
            skLineSegment(sketch, "E81", {"start": v(0, 90) * mm, "end": v(0, 120) * mm, "construction": true});
            skArc(sketch, "E82", {"start": v(15, 120) * mm, "mid": v(0, 135) * mm, "end": v(-15, 120) * mm});
            skLineSegment(sketch, "E83", {"start": v(-15, 120) * mm, "end": v(-15, 108) * mm});
            skLineSegment(sketch, "E84", {"start": v(15, 120) * mm, "end": v(15, 108) * mm});
            skLineSegment(sketch, "E85", {"start": v(-15, 108) * mm, "end": v(-33, 90) * mm});
            skLineSegment(sketch, "E86", {"start": v(15, 108) * mm, "end": v(33, 90) * mm});
            skLineSegment(sketch, "E87", {"start": v(80, 0) * mm, "end": v(-80, 0) * mm, "construction": true});
            skLineSegment(sketch, "E88.MirrorCS", {"start": v(-15, -108) * mm, "end": v(-33, -90) * mm});
            skLineSegment(sketch, "E89.MirrorCS", {"start": v(-15, -120) * mm, "end": v(-15, -108) * mm});
            skCircle(sketch, "E90.MirrorC", {"center": v(0, -120) * mm, "radius": 6 * mm});
            skArc(sketch, "E91.MirrorCS", {"start": v(15, -120) * mm, "mid": v(0, -135) * mm, "end": v(-15, -120) * mm});
            skLineSegment(sketch, "E92.MirrorCS", {"start": v(15, -108) * mm, "end": v(33, -90) * mm});
            skLineSegment(sketch, "E93.MirrorCS", {"start": v(15, -120) * mm, "end": v(15, -108) * mm});
            skSolve(sketch);
        }
        {
            var Q0;
            Q0 = qSketchRegion(id + "F16", true);
            var Q1;
            Q1=makeQuery(id+"F2.opExtrude","CAP_FACE",FACE,{"disambiguationData":[OSD([sQuery(id+"F0.wireOp",EDGE,"E12"),sQuery(id+"F0.wireOp",EDGE,"E13"),sQuery(id+"F0.wireOp",EDGE,"E14"),sQuery(id+"F0.wireOp",EDGE,"E15"),sQuery(id+"F0.wireOp",EDGE,"E17.filletArc"),sQuery(id+"F0.wireOp",EDGE,"E18.filletArc"),sQuery(id+"F0.wireOp",EDGE,"E19.filletArc"),sQuery(id+"F0.wireOp",EDGE,"E20.filletArc"),sQuery(id+"F0.wireOp",EDGE,"E25.0"),sQuery(id+"F0.wireOp",EDGE,"E25.1"),sQuery(id+"F0.wireOp",EDGE,"E25.2"),sQuery(id+"F0.wireOp",EDGE,"E25.3"),sQuery(id+"F0.wireOp",EDGE,"E25.4"),sQuery(id+"F0.wireOp",EDGE,"E25.5"),sQuery(id+"F0.wireOp",EDGE,"E25.6"),sQuery(id+"F0.wireOp",EDGE,"E25.7")])],"isStart":false});
            extrude(context, id + "F17", {"entities" : qUnion([Q0]), "endBound" : BoundingType.UP_TO_SURFACE, "depth" : 25 * mm, "endBoundEntityFace" : qUnion([Q1]), "offsetDistance" : 25 * mm});
        }
    });
